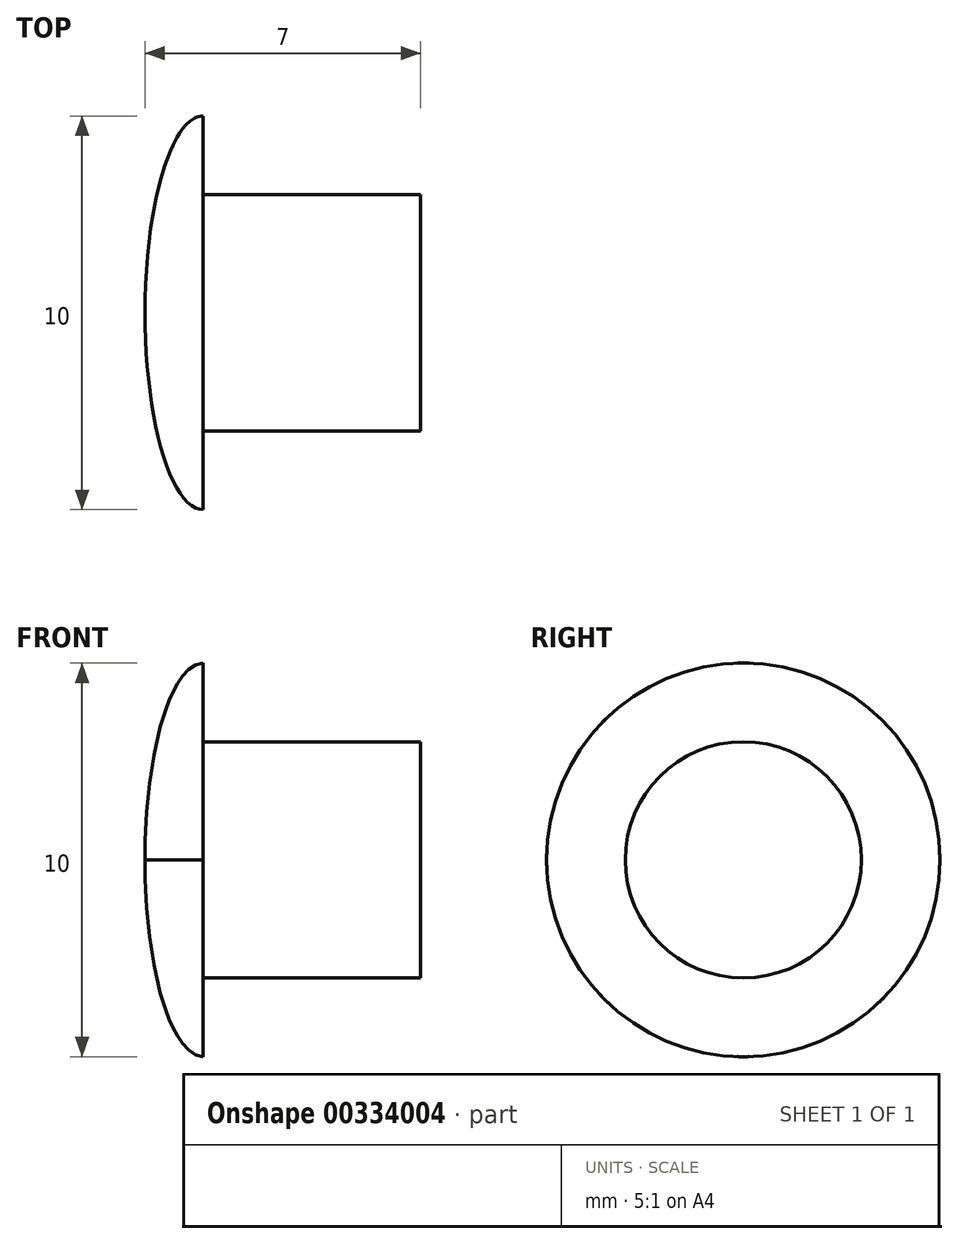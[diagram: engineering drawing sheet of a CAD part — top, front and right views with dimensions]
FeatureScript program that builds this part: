
annotation { "Feature Type Name" : "Feature", "Feature Type Description" : "" }
export const myFeature = defineFeature(function(context is Context, id is Id, definition is map)
    precondition{}
    {
        {
            var Q0;
            Q0=qCreatedBy(makeId("Top.planeOp"),FACE);
            var sketch = newSketch(context, id + "F0", { "sketchPlane" : qUnion([Q0])});
            skLineSegment(sketch, "E0", {"start": v(5.52, 0) * mm, "end": v(5.52, -3) * mm});
            skLineSegment(sketch, "E1", {"start": v(5.52, -3) * mm, "end": v(0, -3) * mm});
            skLineSegment(sketch, "E2", {"start": v(0, -3) * mm, "end": v(0, -5) * mm});
            skLineSegment(sketch, "E3", {"start": v(5.52, 0) * mm, "end": v(-1.48, 0) * mm});
            skEllipticalArc(sketch, "E4", {});
            const initialGuessF0  = {"E4": [0, 0, 0, -1, 0.005, 0.0014791316352784634, 4.71238898038469, 0]};
            skSetInitialGuess(sketch, initialGuessF0);
            skSolve(sketch);
        }
        {
            var Q0;
            Q0=makeQuery(id+"F0.imprint","IMPRINT",FACE,{"disambiguationData":[TD([[makeQuery(id+"F0.imprint","IMPRINT",EDGE,{"derivedFrom":sQuery(id+"F0.wireOp",EDGE,"E0")}),-1.0]])]});
            var Q1;
            Q1=sQuery(id+"F0.wireOp",EDGE,"E3");
            revolve(context, id + "F1", {"entities" : qUnion([Q0]), "axis" : qUnion([Q1]), "revolveType" : RevolveType.FULL});
        }
    });
